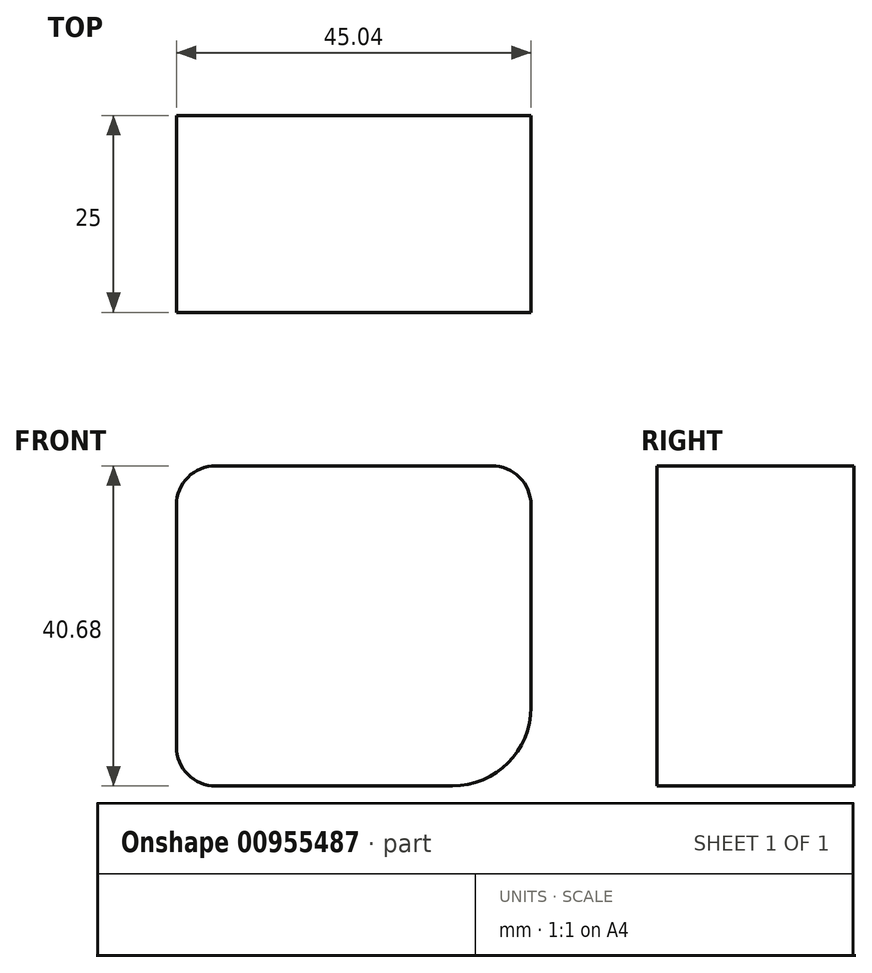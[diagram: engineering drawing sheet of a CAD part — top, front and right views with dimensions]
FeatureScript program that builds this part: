
annotation { "Feature Type Name" : "Feature", "Feature Type Description" : "" }
export const myFeature = defineFeature(function(context is Context, id is Id, definition is map)
    precondition{}
    {
        {
            var Q0;
            Q0=qCreatedBy(makeId("Front.planeOp"),FACE);
            var sketch = newSketch(context, id + "F0", { "sketchPlane" : qUnion([Q0])});
            skLineSegment(sketch, "E0.bottom", {"start": v(-107.66, 40.68) * mm, "end": v(-72.62, 40.68) * mm});
            skLineSegment(sketch, "E0.top", {"start": v(-107.66, 0) * mm, "end": v(-77.62, 0) * mm});
            skLineSegment(sketch, "E0.left", {"start": v(-112.66, 35.68) * mm, "end": v(-112.66, 5) * mm});
            skLineSegment(sketch, "E0.right", {"start": v(-67.62, 35.68) * mm, "end": v(-67.62, 10) * mm});
            skCircle(sketch, "E1", {"center": v(2.21, -1.55) * mm, "radius": 26.96 * mm});
            skCircle(sketch, "E2", {"center": v(-22.16, 9.98) * mm, "radius": 18.77 * mm});
            skCircle(sketch, "E3", {"center": v(18.3, 20.08) * mm, "radius": 24.43 * mm});
            skCircle(sketch, "E4", {"center": v(1.64, -28.5) * mm, "radius": 26.93 * mm});
            skPoint(sketch, "E5.visualSharp", {"position": v(-67.62, 40.68) * mm});
            skArc(sketch, "E5.filletArc", {"start": v(-67.62, 35.68) * mm, "mid": v(-69.09, 39.22) * mm, "end": v(-72.62, 40.68) * mm});
            skPoint(sketch, "E6.visualSharp", {"position": v(-112.66, 40.68) * mm});
            skArc(sketch, "E6.filletArc", {"start": v(-107.66, 40.68) * mm, "mid": v(-111.2, 39.22) * mm, "end": v(-112.66, 35.68) * mm});
            skPoint(sketch, "E7.visualSharp", {"position": v(-112.66, 0) * mm});
            skArc(sketch, "E7.filletArc", {"start": v(-112.66, 5) * mm, "mid": v(-111.2, 1.46) * mm, "end": v(-107.66, 0) * mm});
            skPoint(sketch, "E8.visualSharp", {"position": v(-67.62, 0) * mm});
            skArc(sketch, "E8.filletArc", {"start": v(-77.62, 0) * mm, "mid": v(-70.55, 2.93) * mm, "end": v(-67.62, 10) * mm});
            skSolve(sketch);
        }
        {
            var Q0;
            Q0=makeQuery(id+"F0.imprint","IMPRINT",FACE,{"disambiguationData":[TD([[makeQuery(id+"F0.imprint","IMPRINT",EDGE,{"derivedFrom":sQuery(id+"F0.wireOp",EDGE,"E0.bottom")}),-1.0]])]});
            extrude(context, id + "F1", {"entities" : qUnion([Q0]), "depth" : 25 * mm, "offsetDistance" : 25 * mm});
        }
    });
